# Revit family: Leuchtenträgerschiene - LTS 100 FS.pdf
name_source: partatom
category: Generic Models
revit_build: Autodesk Revit 2017 (Build: 20190508_0315(x64)
units: mm (PartAtom-declared; Revit-internal decimal feet)

## family parameters
Always vertical = Yes
Can host rebar = No
Cut with Voids When Loaded = No
Part Type = Normal
Room Calculation Point = No
Round Connector Dimension = Use Diameter
Shared = No
Work Plane-Based = No

## types (1)
- LTS 100 FS
    Article Type = LTS 100 FS
    Cut's number = 48
    Cut's number 2 = 144
    Cut's number 3 = 60
    Cut's number 4 = 5
    Cut's number 5 = 2
    Cut's space = 125 mm  [stored 0.410105 ft]
    Cut's space 2 = 42 mm  [stored 0.137795 ft]
    Cut's space 3 = 100 mm  [stored 0.328084 ft]
    GTIN = 4012195247135
    Length = 6000 mm  [stored 19.685 ft]
    Manufacturer = OBO BETTERMANN
    Manufacturer Art.No. = 6075024
    Material = <By Category>
    URL = http://www.obo-bettermann.com
    Width = 100 mm  [stored 0.328084 ft]
    Width 1 = 50 mm  [stored 0.164042 ft]

note: [stored X ft] marks values corroborated as IEEE doubles in the binary element streams (Revit-internal decimal feet)

## geometry (parser evidence)
native form markers: Sweep x2
no freeform markers — native parametric forms only
